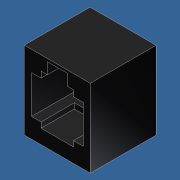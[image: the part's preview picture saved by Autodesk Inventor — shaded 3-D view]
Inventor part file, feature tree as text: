
AUTODESK INVENTOR PART (.ipt)
format: ipt  version: 2012 (Build 160160000, 160)  size: 331,776 bytes
history: native  units: in
note: dims shown in document units (in); Inventor stores cm internally (conversion verified against a paired STEP export)
features: extrude x7, sketch x7, fillet x1
ambient origin geometry x8: Origin, YZ Plane, XZ Plane, XY Plane, X Axis, Y Axis, Z Axis, Center Point
bodies: Solid1 (feature_tree)
feature tree (15):
  extrude  "Extrusion1"  Depth=0.62in
  extrude  "Extrusion2"  Depth=0.022in
  extrude  "Extrusion3"  Depth=0.184in
  extrude  "Extrusion4"  Depth=0.05in
  extrude  "Extrusion5"  Depth=0.048in
  fillet  "Fillet1"  Radius=0.258in
  extrude  "Extrusion6"  Depth=0.076in
  extrude  "Extrusion7"  Depth=0.303in
  sketch  "Sketch1"  dims[d0=0.526in d1=0.62in]
  sketch  "Sketch2"  dims[d2=0.524in d3=0.0in d4=0.022in]
  sketch  "Sketch3"  dims[d5=0.184in d6=0.184in]
  sketch  "Sketch4"  dims[d7=0.09in d9=0.05in]
  sketch  "Sketch5"  dims[d10=0.05in d11=0.048in d13=0.258in]
  sketch  "Sketch6"  dims[d14=0.076in d15=0.076in]
  sketch  "Sketch7"  dims[d16=0.41in d17=0.303in d18=0.076in d19=0.076in d20=0.043in d21=0.114in d22=0.557in d23=0.0in d24=0.005in d25=0.0in d26=0.01in d27=0.01in d28=0.01in d29=0.01in d30=0.015in d31=0.015in d32=0.015in d33=0.0865in d34=0.0865in d35=0.254in d36=0.0in d37=0.15in d38=0.0in d39=0.005in d40=0.043in d41=0.043in d42=0.0in d43=0.0in d44=0.0in d45=0.0in d46=0.087in d47=0.087in d48=0.254in d49=0.0in d50=5.0in d51=0.0in]
